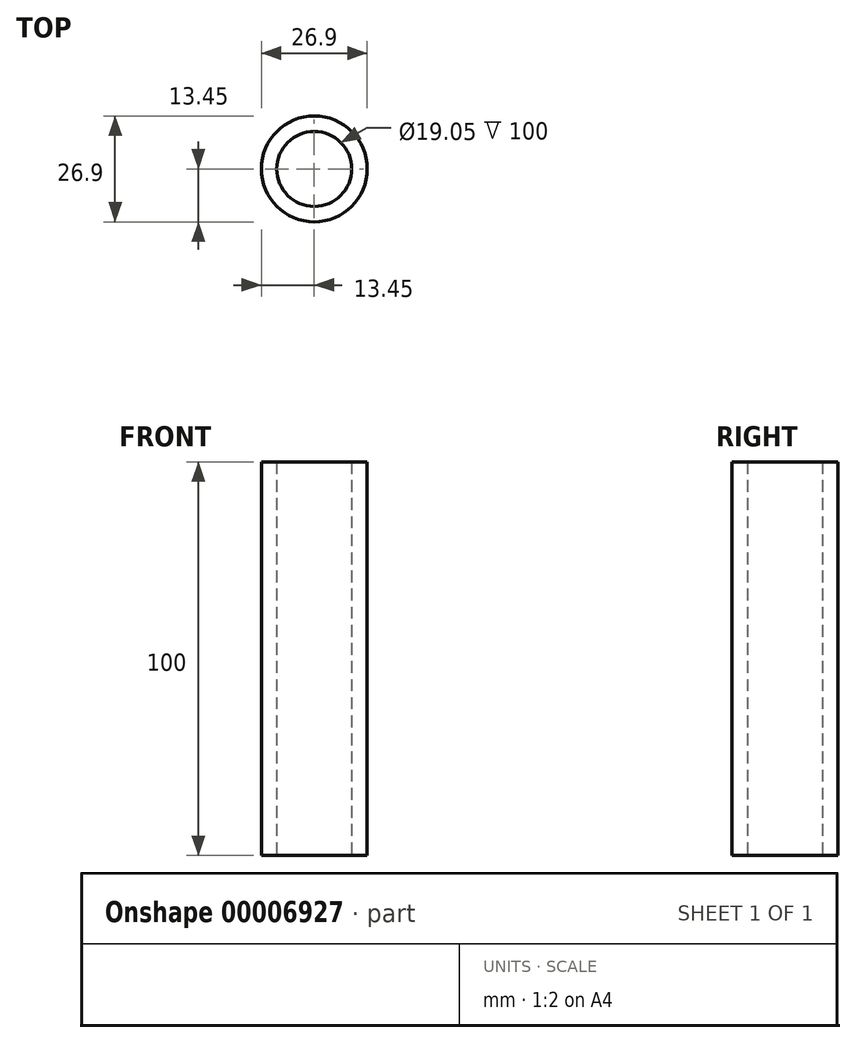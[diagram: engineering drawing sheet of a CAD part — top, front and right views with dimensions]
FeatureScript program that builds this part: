
annotation { "Feature Type Name" : "Feature", "Feature Type Description" : "" }
export const myFeature = defineFeature(function(context is Context, id is Id, definition is map)
    precondition{}
    {
        {
            var Q0;
            Q0=qCreatedBy(makeId("Top.planeOp"),FACE);
            var sketch = newSketch(context, id + "F0", { "sketchPlane" : qUnion([Q0])});
            skCircle(sketch, "E0", {"center": v(0, 0) * mm, "radius": 13.45 * mm});
            skCircle(sketch, "E1", {"center": v(0, 0) * mm, "radius": 9.53 * mm});
            skSolve(sketch);
        }
        {
            var Q0;
            Q0=makeQuery(id+"F0.imprint","IMPRINT",FACE,{"disambiguationData":[TD([[makeQuery(id+"F0.imprint","IMPRINT",EDGE,{"derivedFrom":sQuery(id+"F0.wireOp",EDGE,"E0")}),1.0]])]});
            extrude(context, id + "F1", {"entities" : qUnion([Q0]), "depth" : 100 * mm});
        }
    });
